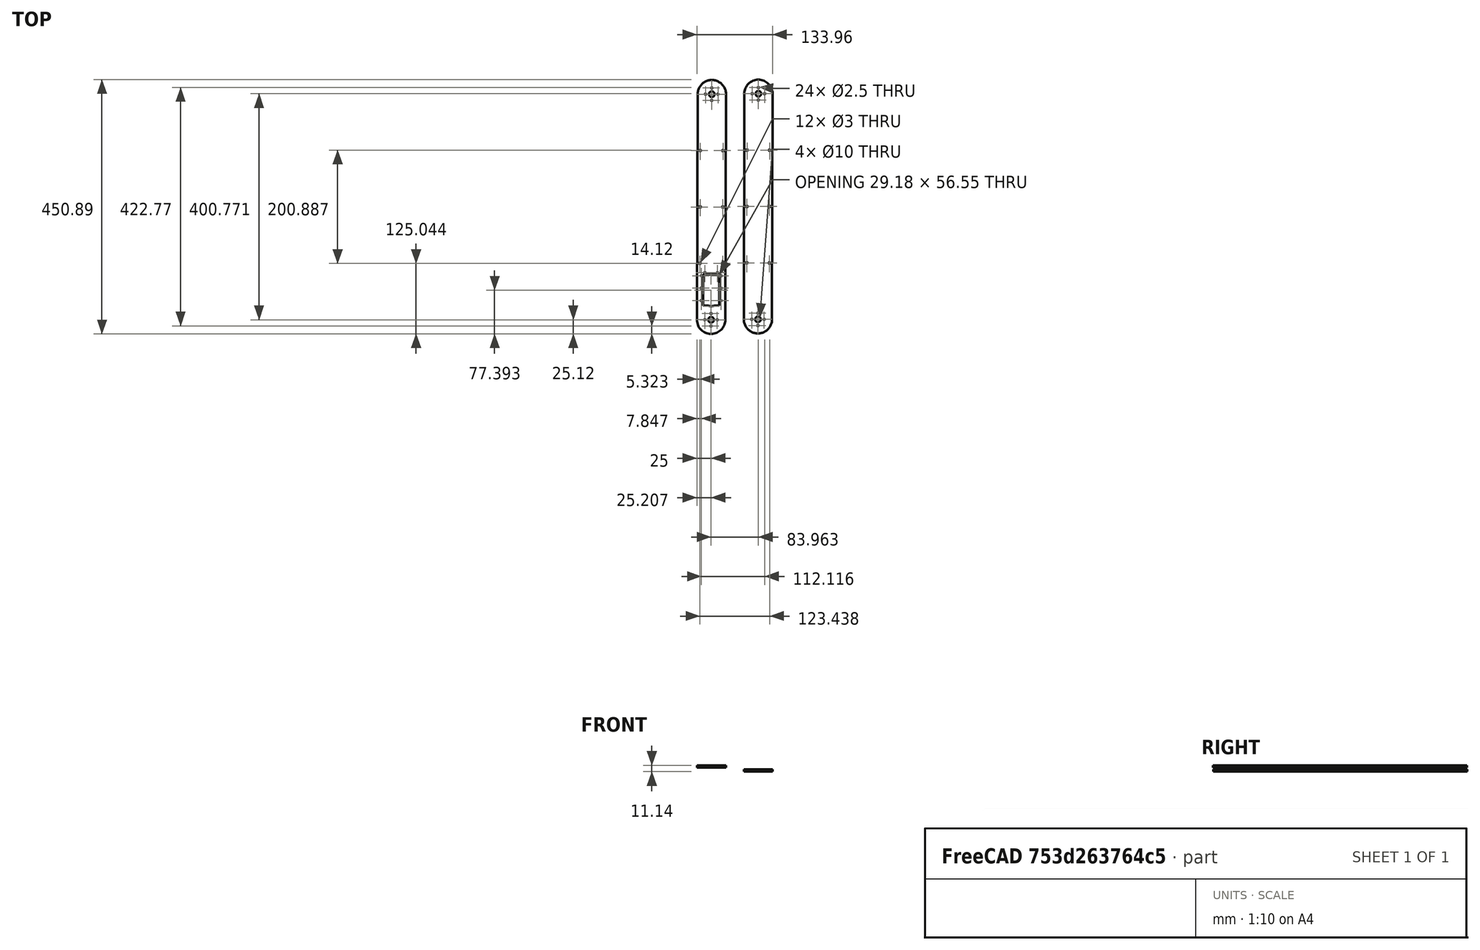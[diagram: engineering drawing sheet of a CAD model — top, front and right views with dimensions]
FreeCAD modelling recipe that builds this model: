
FCSTD DOCUMENT  (FreeCAD 1.0R39109 (Git))
Label: arm_assembly2
License: All rights reserved
LicenseURL: https://en.wikipedia.org/wiki/All_rights_reserved
objects: App::FeaturePython×5, Sketcher::SketchObject×2, PartDesign::Pad×2, PartDesign::Body×2, App::Link×2, Assembly::JointGroup×1, Assembly::AssemblyObject×1
note: 12 computed .brp shape members not serialized (recipe doc carries the construction recipe); baked Part::Feature solids carry a one-line shape summary decoded from their .brp
EXTERNAL_REF file=srv.FCStd obj=Part__Feature

FEATURE [Sketcher::SketchObject] Sketch
  ArcFitTolerance = 1e-06
  AttachmentSupport = -> [XY_Plane]
  FullyConstrained = false
  MakeInternals = false
  MapMode = 5
  sketch-geometry (67):
    g0: LineSegment [constr] StartX=1.5008e-12 StartY=20 StartZ=0 EndX=1.5008e-12 EndY=-20 EndZ=0
    g1: LineSegment [constr] StartX=-2.359e-12 StartY=0 StartZ=0 EndX=-2.359e-12 EndY=400 EndZ=0
    g2: LineSegment [constr] StartX=1.5008e-12 StartY=20 StartZ=0 EndX=1.5008e-12 EndY=25 EndZ=0
    g3: Circle CenterX=-2.359e-12 CenterY=400 CenterZ=0 NormalX=0 NormalY=0 NormalZ=1 AngleXU=0 Radius=5
    g4: Circle CenterX=-2.359e-12 CenterY=400 CenterZ=0 NormalX=0 NormalY=0 NormalZ=1 AngleXU=0 Radius=2
    g5: Circle CenterX=-10.9997 CenterY=400 CenterZ=0 NormalX=0 NormalY=0 NormalZ=1 AngleXU=0 Radius=1.25
    g6: Circle CenterX=0 CenterY=389 CenterZ=0 NormalX=0 NormalY=0 NormalZ=1 AngleXU=0 Radius=1.25
    g7: Circle CenterX=10.9997 CenterY=400 CenterZ=0 NormalX=0 NormalY=0 NormalZ=1 AngleXU=0 Radius=1.25
    g8: Circle CenterX=0 CenterY=411 CenterZ=0 NormalX=0 NormalY=0 NormalZ=1 AngleXU=0 Radius=1.25
    g9: LineSegment [constr] StartX=0 StartY=-5 StartZ=0 EndX=0 EndY=5.99996 EndZ=0
    g10: Circle [constr] CenterX=0 CenterY=0 CenterZ=0 NormalX=0 NormalY=0 NormalZ=1 AngleXU=0 Radius=14
    g11: LineSegment [constr] StartX=0 StartY=0 StartZ=0 EndX=25.23 EndY=0 EndZ=0
    g12: Circle [constr] CenterX=0 CenterY=-3.8e-05 CenterZ=0 NormalX=0 NormalY=0 NormalZ=1 AngleXU=0 Radius=11
    g13: Circle CenterX=0 CenterY=0 CenterZ=0 NormalX=0 NormalY=0 NormalZ=1 AngleXU=0 Radius=5
    g14: Circle CenterX=10.9997 CenterY=0 CenterZ=0 NormalX=0 NormalY=0 NormalZ=1 AngleXU=0 Radius=1.25
    g15: Circle CenterX=-10.9997 CenterY=0 CenterZ=0 NormalX=0 NormalY=0 NormalZ=1 AngleXU=0 Radius=1.25
    g16: Circle CenterX=0 CenterY=-10.9997 CenterZ=0 NormalX=0 NormalY=0 NormalZ=1 AngleXU=0 Radius=1.25
    g17: Circle CenterX=0 CenterY=11 CenterZ=0 NormalX=0 NormalY=0 NormalZ=1 AngleXU=0 Radius=1.25
    g18: LineSegment [constr] StartX=0 StartY=0 StartZ=0 EndX=-25 EndY=0 EndZ=0
    g19: LineSegment [constr] StartX=20.1368 StartY=86.0999 StartZ=0 EndX=20.1368 EndY=24.9999 EndZ=0
    g20: LineSegment [constr] StartX=0.036848 StartY=80.5 StartZ=0 EndX=14.5368 EndY=80.5 EndZ=0
    g21: LineSegment StartX=14.5368 StartY=80.5 StartZ=0 EndX=-14.4632 EndY=80.5 EndZ=0
    g22: LineSegment StartX=14.5368 StartY=80.5 StartZ=0 EndX=14.5368 EndY=24.9999 EndZ=0
    g23: Circle CenterX=11.0368 CenterY=83.3 CenterZ=0 NormalX=0 NormalY=0 NormalZ=1 AngleXU=0 Radius=1.25
    g24: Circle CenterX=17.3368 CenterY=78 CenterZ=0 NormalX=0 NormalY=0 NormalZ=1 AngleXU=0 Radius=1.25
    g25: LineSegment [constr] StartX=-20.0632 StartY=86.0999 StartZ=0 EndX=20.1368 EndY=86.0999 EndZ=0
    g26: Circle CenterX=17.3368 CenterY=56 CenterZ=0 NormalX=0 NormalY=0 NormalZ=1 AngleXU=0 Radius=1.25
    g27: Circle CenterX=17.3368 CenterY=34 CenterZ=0 NormalX=0 NormalY=0 NormalZ=1 AngleXU=0 Radius=1.25
    g28: Circle [constr] CenterX=0.036848 CenterY=37.9999 CenterZ=0 NormalX=0 NormalY=0 NormalZ=1 AngleXU=0 Radius=14
    g29: ArcOfCircle CenterX=0.036848 CenterY=37.9999 CenterZ=0 NormalX=0 NormalY=0 NormalZ=1 AngleXU=0 Radius=14 StartAngle=4.33214 EndAngle=5.09264
    g30: LineSegment StartX=5.233 StartY=24.9999 StartZ=0 EndX=14.5368 EndY=24.9999 EndZ=0
    g31: LineSegment [constr] StartX=14.5368 StartY=24.9999 StartZ=0 EndX=20.1368 EndY=24.9999 EndZ=0
    g32: LineSegment [constr] StartX=17.3368 StartY=56 StartZ=0 EndX=-17.2632 EndY=56 EndZ=0
    g33: LineSegment [constr] StartX=-20.0632 StartY=24.9999 StartZ=0 EndX=-20.0632 EndY=86.0999 EndZ=0
    g34: LineSegment StartX=-14.4632 StartY=80.5 StartZ=0 EndX=-14.4632 EndY=24.9999 EndZ=0
    g35: Circle CenterX=-17.2632 CenterY=78 CenterZ=0 NormalX=0 NormalY=0 NormalZ=1 AngleXU=0 Radius=1.25
    g36: Circle CenterX=-10.9632 CenterY=83.3 CenterZ=0 NormalX=0 NormalY=0 NormalZ=1 AngleXU=0 Radius=1.25
    g37: Circle CenterX=-17.2632 CenterY=56 CenterZ=0 NormalX=0 NormalY=0 NormalZ=1 AngleXU=0 Radius=1.25
    g38: Circle CenterX=-17.2632 CenterY=34 CenterZ=0 NormalX=0 NormalY=0 NormalZ=1 AngleXU=0 Radius=1.25
    g39: LineSegment StartX=-14.4632 StartY=24.9999 StartZ=0 EndX=-5.15931 EndY=24.9999 EndZ=0
    g40: LineSegment [constr] StartX=-20.0632 StartY=24.9999 StartZ=0 EndX=-14.4632 EndY=24.9999 EndZ=0
    g41: ArcOfCircle CenterX=0.115002 CenterY=3.75548e-06 CenterZ=0 NormalX=0 NormalY=0 NormalZ=1 AngleXU=0 Radius=25.115 StartAngle=3.14159 EndAngle=6.28319
    g42: ArcOfCircle CenterX=0.115002 CenterY=399.959 CenterZ=0 NormalX=0 NormalY=0 NormalZ=1 AngleXU=0 Radius=25.115 StartAngle=0 EndAngle=3.14159
    g43: LineSegment StartX=-25 StartY=3.75548e-06 StartZ=0 EndX=-25 EndY=399.959 EndZ=0
    g44: LineSegment StartX=25.23 StartY=3.75548e-06 StartZ=0 EndX=25.23 EndY=399.959 EndZ=0
    g45: LineSegment [constr] StartX=25.23 StartY=199.98 StartZ=0 EndX=-25 EndY=199.98 EndZ=0
    g46: LineSegment [constr] StartX=25.23 StartY=199.98 StartZ=0 EndX=55.23 EndY=199.98 EndZ=0
    g47: LineSegment [constr] StartX=25.23 StartY=0 StartZ=0 EndX=55.23 EndY=0 EndZ=0
    g48: LineSegment [constr] StartX=55.23 StartY=0 StartZ=0 EndX=55.23 EndY=199.98 EndZ=0
    g49: LineSegment [constr] StartX=55.23 StartY=99.9898 StartZ=0 EndX=25.23 EndY=99.9898 EndZ=0
    g50: LineSegment [constr] StartX=25.23 StartY=99.9898 StartZ=0 EndX=-25 EndY=99.9898 EndZ=0
    g51: LineSegment [constr] StartX=25.23 StartY=399.959 StartZ=0 EndX=55.23 EndY=399.959 EndZ=0
    g52: LineSegment [constr] StartX=55.23 StartY=399.959 StartZ=0 EndX=55.23 EndY=199.98 EndZ=0
    g53: LineSegment [constr] StartX=55.23 StartY=299.969 StartZ=0 EndX=25.23 EndY=299.969 EndZ=0
    g54: LineSegment [constr] StartX=25.23 StartY=299.969 StartZ=0 EndX=-25 EndY=299.969 EndZ=0
    g55: LineSegment [constr] StartX=-25 StartY=299.969 StartZ=0 EndX=-20 EndY=299.969 EndZ=0
    g56: LineSegment [constr] StartX=-20 StartY=299.969 StartZ=0 EndX=-20 EndY=199.98 EndZ=0
    g57: LineSegment [constr] StartX=-20 StartY=199.98 StartZ=0 EndX=-20 EndY=99.9898 EndZ=0
    g58: LineSegment [constr] StartX=25.23 StartY=299.969 StartZ=0 EndX=20.23 EndY=299.969 EndZ=0
    g59: LineSegment [constr] StartX=20.23 StartY=299.969 StartZ=0 EndX=20.23 EndY=199.98 EndZ=0
    g60: LineSegment [constr] StartX=20.23 StartY=199.98 StartZ=0 EndX=20.23 EndY=99.9898 EndZ=0
    g61: Circle CenterX=-20 CenterY=299.969 CenterZ=0 NormalX=0 NormalY=0 NormalZ=1 AngleXU=0 Radius=1.5
    g62: Circle CenterX=20.23 CenterY=299.969 CenterZ=0 NormalX=0 NormalY=0 NormalZ=1 AngleXU=0 Radius=1.5
    g63: Circle CenterX=-20 CenterY=199.98 CenterZ=0 NormalX=0 NormalY=0 NormalZ=1 AngleXU=0 Radius=1.5
    g64: Circle CenterX=20.23 CenterY=199.98 CenterZ=0 NormalX=0 NormalY=0 NormalZ=1 AngleXU=0 Radius=1.5
    g65: Circle CenterX=-20 CenterY=99.9898 CenterZ=0 NormalX=0 NormalY=0 NormalZ=1 AngleXU=0 Radius=1.5
    g66: Circle CenterX=20.23 CenterY=99.9898 CenterZ=0 NormalX=0 NormalY=0 NormalZ=1 AngleXU=0 Radius=1.5
  constraints (132):
    c: Vertical(g0)
    c: Vertical(g1)
    c: Coincident(g2,g0)
    c: Vertical(g2)
    c: Diameter(g3) = 10
    c: Coincident(g3,g1)
    c: Diameter(g4) = 4
    c: Coincident(g4,g1)
    c: Diameter(g8) = 2.5
    c: Diameter(g5) = 2.5
    c: Diameter(g6) = 2.5
    c: Diameter(g7) = 2.5
    c: Vertical(g9)
    c: Diameter(g10) = 28
    c: Coincident(g18,g10)
    c: Horizontal(g18)
    c: Coincident(g11,g10)
    c: Horizontal(g11)
    c: Diameter(g12) = 22
    c: Diameter(g13) = 10
    c: Coincident(g13,g10)
    c: Diameter(g17) = 2.5
    c: Diameter(g15) = 2.5
    c: Diameter(g16) = 2.5
    c: Diameter(g14) = 2.5
    c: Coincident(g25,g19)
    c: Coincident(g33,g25)
    c: Horizontal(g25)
    c: Vertical(g19)
    c: Vertical(g33)
    c: Distance(g19,g33) = 40.2
    c: Distance(g25,g33) = 61.1
    c: Diameter(g29) = 28
    c: Horizontal(g20)
    c: Coincident(g21,g20)
    c: Horizontal(g21)
    c: Coincident(g34,g21)
    c: Vertical(g34)
    c: Coincident(g22,g20)
    c: Vertical(g22)
    c: Diameter(g23) = 2.5
    c: Equal(g23,g36)
    c: Equal(g23,g27)
    c: Equal(g23,g38)
    c: Equal(g23,g37)
    c: Equal(g23,g35)
    c: Equal(g23,g24)
    c: Equal(g23,g26)
    c: Coincident(g28,g29)
    c: PointOnObject(g29,g28)
    c: Coincident(g30,g29)
    c: Coincident(g30,g22)
    c: Horizontal(g30)
    c: Coincident(g31,g22)
    c: Coincident(g31,g19)
    c: Horizontal(g31)
    c: Coincident(g39,g34)
    c: Coincident(g39,g29)
    c: Horizontal(g39)
    c: Coincident(g40,g33)
    c: Coincident(g40,g34)
    c: Horizontal(g40)
    c: Coincident(g32,g26)
    c: Coincident(g32,g37)
    c: Horizontal(g32)
    c: DistanceY(g28,g1) = 362
    c: Tangent(g41,g43) = 1.5708
    c: Tangent(g41,g44) = -1.5708
    c: Tangent(g42,g43) = 1.5708
    c: Tangent(g42,g44) = -1.5708
    c: Equal(g41,g42)
    c: Symmetric(g44,g44,g45)
    c: Symmetric(g43,g43,g45)
    c: Horizontal(g45)
    c: Distance(g46) = 30
    c: Horizontal(g46)
    c: Coincident(g46,g45)
    c: Distance(g47) = 30
    c: Horizontal(g47)
    c: Coincident(g47,g11)
    c: PointOnObject(g47,g-1)
    c: Coincident(g48,g47)
    c: Coincident(g48,g46)
    c: Vertical(g48)
    c: Symmetric(g48,g48,g49)
    c: PointOnObject(g49,g44)
    c: Horizontal(g49)
    c: Coincident(g50,g49)
    c: PointOnObject(g50,g43)
    c: Horizontal(g50)
    c: Distance(g51) = 30
    c: Horizontal(g51)
    c: Coincident(g51,g42)
    c: Coincident(g52,g51)
    c: Coincident(g52,g46)
    c: Symmetric(g52,g52,g53)
    c: PointOnObject(g53,g44)
    c: Horizontal(g53)
    c: Coincident(g54,g53)
    c: PointOnObject(g54,g43)
    c: Horizontal(g54)
    c: Distance(g55) = 5
    c: Coincident(g55,g54)
    c: PointOnObject(g55,g54)
    c: Coincident(g56,g55)
    c: PointOnObject(g56,g45)
    c: Vertical(g56)
    c: Coincident(g57,g56)
    c: PointOnObject(g57,g50)
    c: Vertical(g57)
    c: Distance(g58) = 5
    c: Coincident(g58,g53)
    c: PointOnObject(g58,g54)
    c: Coincident(g59,g58)
    c: PointOnObject(g59,g45)
    c: Vertical(g59)
    c: Coincident(g60,g59)
    c: PointOnObject(g60,g50)
    c: Vertical(g60)
    c: Coincident(g61,g55)
    c: Diameter(g61) = 3
    c: Coincident(g62,g58)
    c: Equal(g61,g62)
    c: Coincident(g63,g56)
    c: Equal(g61,g63)
    c: Coincident(g64,g59)
    c: Equal(g63,g64)
    c: Coincident(g65,g57)
    c: Equal(g63,g65)
    c: Coincident(g66,g60)
    c: Equal(g65,g66)
    c: DistanceY(g41,g28) = 37.9999
FEATURE [Sketcher::SketchObject] Sketch001
  ArcFitTolerance = 1e-06
  FullyConstrained = false
  MakeInternals = false
  MapMode = 5
  sketch-geometry (41):
    g0: Circle [constr] CenterX=7e-16 CenterY=0.000303 CenterZ=0 NormalX=0 NormalY=0 NormalZ=1 AngleXU=0 Radius=14
    g1: LineSegment [constr] StartX=7e-16 StartY=0.000303 StartZ=0 EndX=7e-16 EndY=400.001 EndZ=0
    g2: Circle CenterX=7e-16 CenterY=400.001 CenterZ=0 NormalX=0 NormalY=0 NormalZ=1 AngleXU=0 Radius=5
    g3: Circle CenterX=7e-16 CenterY=0 CenterZ=0 NormalX=0 NormalY=0 NormalZ=1 AngleXU=0 Radius=5
    g4: Circle CenterX=7e-16 CenterY=400.001 CenterZ=0 NormalX=0 NormalY=0 NormalZ=1 AngleXU=0 Radius=2
    g5: Circle CenterX=7e-16 CenterY=0.000303 CenterZ=0 NormalX=0 NormalY=0 NormalZ=1 AngleXU=0 Radius=2
    g6: Circle [constr] CenterX=0 CenterY=0 CenterZ=0 NormalX=0 NormalY=0 NormalZ=1 AngleXU=0 Radius=11
    g7: ArcOfCircle CenterX=7e-16 CenterY=0 CenterZ=0 NormalX=0 NormalY=0 NormalZ=1 AngleXU=0 Radius=25 StartAngle=3.14159 EndAngle=6.28319
    g8: ArcOfCircle CenterX=7e-16 CenterY=400.001 CenterZ=0 NormalX=0 NormalY=0 NormalZ=1 AngleXU=0 Radius=25 StartAngle=6e-16 EndAngle=3.14159
    g9: LineSegment StartX=-25 StartY=-8e-15 StartZ=0 EndX=-25 EndY=400.001 EndZ=0
    g10: LineSegment StartX=25 StartY=0 StartZ=0 EndX=25 EndY=400.001 EndZ=0
    g11: Circle CenterX=10.9997 CenterY=400.001 CenterZ=0 NormalX=0 NormalY=0 NormalZ=1 AngleXU=0 Radius=1.25
    g12: Circle CenterX=0 CenterY=411.001 CenterZ=0 NormalX=0 NormalY=0 NormalZ=1 AngleXU=0 Radius=1.25
    g13: Circle CenterX=-10.9997 CenterY=400.001 CenterZ=0 NormalX=0 NormalY=0 NormalZ=1 AngleXU=0 Radius=1.25
    g14: Circle CenterX=0 CenterY=389.001 CenterZ=0 NormalX=0 NormalY=0 NormalZ=1 AngleXU=0 Radius=1.25
    g15: Circle CenterX=10.9997 CenterY=0.000303 CenterZ=0 NormalX=0 NormalY=0 NormalZ=1 AngleXU=0 Radius=1.25
    g16: Circle CenterX=0 CenterY=11 CenterZ=0 NormalX=0 NormalY=0 NormalZ=1 AngleXU=0 Radius=1.25
    g17: Circle CenterX=-10.9997 CenterY=0.000303 CenterZ=0 NormalX=0 NormalY=0 NormalZ=1 AngleXU=0 Radius=1.25
    g18: Circle CenterX=0 CenterY=-10.9994 CenterZ=0 NormalX=0 NormalY=0 NormalZ=1 AngleXU=0 Radius=1.25
    g19: LineSegment [constr] StartX=25 StartY=200 StartZ=0 EndX=-25 EndY=200 EndZ=0
    g20: LineSegment [constr] StartX=25 StartY=200 StartZ=0 EndX=55 EndY=200 EndZ=0
    g21: LineSegment [constr] StartX=25 StartY=0 StartZ=0 EndX=55 EndY=0 EndZ=0
    g22: LineSegment [constr] StartX=25 StartY=400.001 StartZ=0 EndX=55 EndY=400.001 EndZ=0
    g23: LineSegment [constr] StartX=55 StartY=200 StartZ=0 EndX=55 EndY=400.001 EndZ=0
    g24: LineSegment [constr] StartX=55 StartY=200 StartZ=0 EndX=55 EndY=0 EndZ=0
    g25: LineSegment [constr] StartX=55 StartY=100 StartZ=0 EndX=25 EndY=100 EndZ=0
    g26: LineSegment [constr] StartX=25 StartY=100 StartZ=0 EndX=-25 EndY=100 EndZ=0
    g27: LineSegment [constr] StartX=55 StartY=300 StartZ=0 EndX=25 EndY=300 EndZ=0
    g28: LineSegment [constr] StartX=25 StartY=300 StartZ=0 EndX=-25 EndY=300 EndZ=0
    g29: LineSegment [constr] StartX=-25 StartY=300 StartZ=0 EndX=-20 EndY=300 EndZ=0
    g30: LineSegment [constr] StartX=-20 StartY=300 StartZ=0 EndX=-20 EndY=200 EndZ=0
    g31: LineSegment [constr] StartX=-20 StartY=200 StartZ=0 EndX=-20 EndY=100 EndZ=0
    g32: LineSegment [constr] StartX=25 StartY=100 StartZ=0 EndX=20 EndY=100 EndZ=0
    g33: LineSegment [constr] StartX=20 StartY=100 StartZ=0 EndX=20 EndY=200 EndZ=0
    g34: LineSegment [constr] StartX=20 StartY=200 StartZ=0 EndX=20 EndY=300 EndZ=0
    g35: Circle CenterX=-20 CenterY=300 CenterZ=0 NormalX=0 NormalY=0 NormalZ=1 AngleXU=0 Radius=1.5
    g36: Circle CenterX=20 CenterY=300 CenterZ=0 NormalX=0 NormalY=0 NormalZ=1 AngleXU=0 Radius=1.5
    g37: Circle CenterX=-20 CenterY=200 CenterZ=0 NormalX=0 NormalY=0 NormalZ=1 AngleXU=0 Radius=1.5
    g38: Circle CenterX=20 CenterY=200 CenterZ=0 NormalX=0 NormalY=0 NormalZ=1 AngleXU=0 Radius=1.5
    g39: Circle CenterX=-20 CenterY=100 CenterZ=0 NormalX=0 NormalY=0 NormalZ=1 AngleXU=0 Radius=1.5
    g40: Circle CenterX=20 CenterY=100 CenterZ=0 NormalX=0 NormalY=0 NormalZ=1 AngleXU=0 Radius=1.5
  constraints (85):
    c: Diameter(g0) = 28
    c: Coincident(g1,g0)
    c: Vertical(g1)
    c: Coincident(g2,g1)
    c: Diameter(g3) = 10
    c: Diameter(g4) = 4
    c: Coincident(g4,g1)
    c: Diameter(g5) = 4
    c: Coincident(g5,g0)
    c: Diameter(g6) = 22
    c: Tangent(g7,g9) = 1.5708
    c: Tangent(g7,g10) = -1.5708
    c: Tangent(g8,g9) = 1.5708
    c: Tangent(g8,g10) = -1.5708
    c: Equal(g7,g8)
    c: Radius(g7) = 25
    c: Coincident(g7,g3)
    c: Coincident(g8,g1)
    c: Vertical(g9)
    c: Diameter(g12) = 2.5
    c: Diameter(g13) = 2.5
    c: Diameter(g14) = 2.5
    c: Diameter(g11) = 2.5
    c: Diameter(g16) = 2.5
    c: Diameter(g17) = 2.5
    c: Diameter(g18) = 2.5
    c: Diameter(g15) = 2.5
    c: Symmetric(g10,g10,g19)
    c: Symmetric(g9,g9,g19)
    c: Distance(g20) = 30
    c: Horizontal(g20)
    c: Coincident(g20,g19)
    c: Distance(g21) = 30
    c: Horizontal(g21)
    c: Coincident(g21,g7)
    c: PointOnObject(g21,g-1)
    c: Distance(g22) = 30
    c: Horizontal(g22)
    c: Coincident(g22,g8)
    c: Coincident(g23,g20)
    c: Coincident(g23,g22)
    c: Coincident(g24,g20)
    c: Coincident(g24,g21)
    c: Symmetric(g24,g24,g25)
    c: PointOnObject(g25,g10)
    c: Horizontal(g25)
    c: Coincident(g26,g25)
    c: PointOnObject(g26,g9)
    c: Horizontal(g26)
    c: Symmetric(g23,g23,g27)
    c: PointOnObject(g27,g10)
    c: Horizontal(g27)
    c: Coincident(g28,g27)
    c: PointOnObject(g28,g9)
    c: Horizontal(g28)
    c: Distance(g29) = 5
    c: Horizontal(g29)
    c: Coincident(g29,g28)
    c: Coincident(g30,g29)
    c: PointOnObject(g30,g19)
    c: Vertical(g30)
    c: Coincident(g31,g30)
    c: PointOnObject(g31,g26)
    c: Vertical(g31)
    c: Distance(g32) = 5
    c: Horizontal(g32)
    c: Coincident(g32,g25)
    c: Coincident(g33,g32)
    c: PointOnObject(g33,g19)
    c: Vertical(g33)
    c: Coincident(g34,g33)
    c: PointOnObject(g34,g28)
    c: Vertical(g34)
    c: Diameter(g35) = 3
    c: Coincident(g35,g29)
    c: Coincident(g36,g34)
    c: Equal(g35,g36)
    c: Coincident(g37,g30)
    c: Equal(g35,g37)
    c: Coincident(g38,g33)
    c: Equal(g37,g38)
    c: Coincident(g39,g31)
    c: Equal(g37,g39)
    c: Coincident(g40,g32)
    c: Equal(g39,g40)
FEATURE [PartDesign::Pad] Pad
  Direction = (0,0,1)
  Length = 4
  Length2 = 10
  Profile = -> Sketch
  ReferenceAxis = -> Sketch [N_Axis]
  Refine = true
  Suppressed = false
  Type = 0
FEATURE [PartDesign::Body] Body  label="arm_low_1"
  AllowCompound = false
  Group = -> [Sketch,Pad]
  Origin = -> Origin
  Placement = pos=(0,0,25.3) rot=(0,0,-1;0.003227rad)
  Tip = -> Pad
FEATURE [PartDesign::Pad] Pad001
  Direction = (0,0,1)
  Length = 4
  Length2 = 10
  Profile = -> Sketch001
  ReferenceAxis = -> Sketch001 [N_Axis]
  Refine = true
  Suppressed = false
  Type = 0
FEATURE [PartDesign::Body] Body001  label="arm_high_1"
  AllowCompound = false
  Group = -> [Sketch001,Pad001]
  Origin = -> Origin001
  Placement = pos=(83.1539,0.770773,18.1622) rot=(0,0,-1;0.002023rad)
  Tip = -> Pad001
FEATURE [App::Link] DC05_M01_DUMMY
  LinkedObject = -> <external srv.FCStd>#Part__Feature
FEATURE [App::FeaturePython] GroundedJoint  # Assembly grounded joint (typed FeaturePython)
  ObjectToGround = -> DC05_M01_DUMMY
FEATURE [App::FeaturePython] Joint  label="Revolute"  # Assembly joint (typed FeaturePython)
  Activated = true
  AngleMax = 0
  AngleMin = 0
  Detach1 = false
  Detach2 = false
  Distance = 0
  Distance2 = 0
  EnableAngleMax = false
  EnableAngleMin = false
  EnableLengthMax = false
  EnableLengthMin = false
  JointType = 1 (Revolute)
  LengthMax = 0
  LengthMin = 0
  Placement2 = pos=(0,0,25.3) rot=(-0.707107,0.707107,0;3.14159rad)
  Reference1 = -> Assembly [Body.Face11,Body.Edge2]
  Reference2 = -> Assembly [DC05_M01_DUMMY.Face269,DC05_M01_DUMMY.Edge1]
FEATURE [App::Link] DC05_M01_DUMMY001
  LinkPlacement = pos=(0.159487,37.9996,9.05) rot=(0,0,1;3.13836rad)
  LinkedObject = -> <external srv.FCStd>#Part__Feature
  Placement = pos=(0.159487,37.9996,9.05) rot=(0,0,1;3.13836rad)
FEATURE [App::FeaturePython] Joint002  label="Distance"  # Assembly joint (typed FeaturePython)
  Activated = true
  AngleMax = 0
  AngleMin = 0
  Detach1 = false
  Detach2 = false
  Distance = 0
  Distance2 = 0
  EnableAngleMax = false
  EnableAngleMin = false
  EnableLengthMax = false
  EnableLengthMin = false
  JointType = 5 (Distance)
  LengthMax = 0
  LengthMin = 0
  Placement1 = pos=(0.00149626,-23.2403,17) rot=(0,0,1;0rad)
  Placement2 = pos=(-10.9997,0,2) rot=(0,0,1;0rad)
  Reference1 = -> Assembly [DC05_M01_DUMMY001.Face128,DC05_M01_DUMMY001.Vertex405]
  Reference2 = -> Assembly [Body.Face29,Body.Edge23]
FEATURE [App::FeaturePython] Joint003  label="Distance001"  # Assembly joint (typed FeaturePython)
  Activated = true
  AngleMax = 0
  AngleMin = 0
  Detach1 = false
  Detach2 = false
  Distance = -55.5
  Distance2 = 0
  EnableAngleMax = false
  EnableAngleMin = false
  EnableLengthMax = false
  EnableLengthMin = false
  JointType = 5 (Distance)
  LengthMax = 0
  LengthMin = 0
  Placement1 = pos=(3.76754e-09,-42.5,18.25) rot=(1,0,0;1.5708rad)
  Placement2 = pos=(-9.81123,24.9999,2) rot=(-1,0,0;1.5708rad)
  Reference1 = -> Assembly [DC05_M01_DUMMY001.Face34,DC05_M01_DUMMY001.Face34]
  Reference2 = -> Assembly [Body.Face7,Body.Face7]
FEATURE [App::FeaturePython] Joint004  label="Distance002"  # Assembly joint (typed FeaturePython)
  Activated = true
  AngleMax = 0
  AngleMin = 0
  Detach1 = false
  Detach2 = false
  Distance = -28.5
  Distance2 = 0
  EnableAngleMax = false
  EnableAngleMin = false
  EnableLengthMax = false
  EnableLengthMin = false
  JointType = 5 (Distance)
  LengthMax = 0
  LengthMin = 0
  Placement1 = pos=(-14.5,-15.25,18.25) rot=(0.57735,-0.57735,-0.57735;2.0944rad)
  Placement2 = pos=(0.036848,37.9999,2) rot=(0,0,1;0rad)
  Reference1 = -> Assembly [DC05_M01_DUMMY001.Face46,DC05_M01_DUMMY001.Face46]
  Reference2 = -> Assembly [Body.Face8,Body.Face8]
FEATURE [Assembly::JointGroup] Joints
  Group = -> [GroundedJoint,Joint,Joint002,Joint003,Joint004]
FEATURE [Assembly::AssemblyObject] Assembly
  Group = -> [Joints,Body,Body001,DC05_M01_DUMMY,GroundedJoint,Joint,DC05_M01_DUMMY001,Joint002,Joint003,Joint004]
  Origin = -> Origin003
  Type = Assembly
